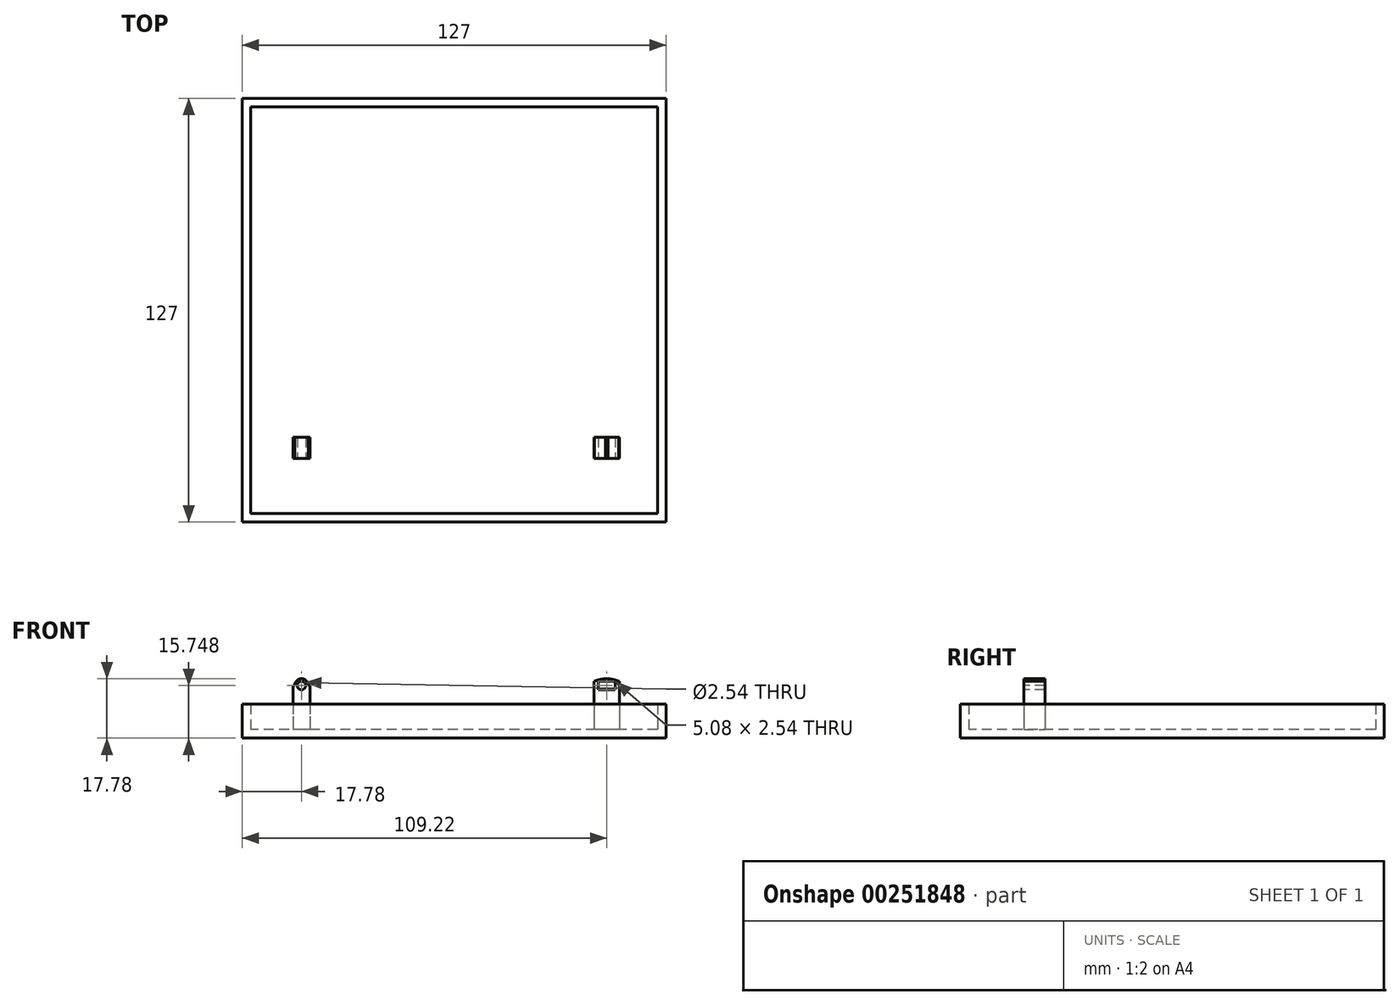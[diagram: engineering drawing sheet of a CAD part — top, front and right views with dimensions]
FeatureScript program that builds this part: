
annotation { "Feature Type Name" : "Feature", "Feature Type Description" : "" }
export const myFeature = defineFeature(function(context is Context, id is Id, definition is map)
    precondition{}
    {
        {
            var Q0;
            Q0=qCreatedBy(makeId("Top.planeOp"),FACE);
            var sketch = newSketch(context, id + "F0", { "sketchPlane" : qUnion([Q0])});
            skLineSegment(sketch, "E0.bottom", {"start": v(63.5, 63.5) * mm, "end": v(-63.5, 63.5) * mm});
            skLineSegment(sketch, "E0.top", {"start": v(63.5, -63.5) * mm, "end": v(-63.5, -63.5) * mm});
            skLineSegment(sketch, "E0.left", {"start": v(63.5, 63.5) * mm, "end": v(63.5, -63.5) * mm});
            skLineSegment(sketch, "E0.right", {"start": v(-63.5, 63.5) * mm, "end": v(-63.5, -63.5) * mm});
            skPoint(sketch, "E0.middle", {"position": v(0, 0) * mm});
            skSolve(sketch);
        }
        {
            var Q0;
            Q0 = qSketchRegion(id + "F0", true);
            extrude(context, id + "F1", {"entities" : qUnion([Q0]), "depth" : 2.54 * mm});
        }
        {
            var Q0;
            Q0=makeQuery(id+"F1.opExtrude","CAP_FACE",FACE,{"disambiguationData":[OSD([sQuery(id+"F0.wireOp",EDGE,"E0.bottom"),sQuery(id+"F0.wireOp",EDGE,"E0.top"),sQuery(id+"F0.wireOp",EDGE,"E0.left"),sQuery(id+"F0.wireOp",EDGE,"E0.right")])],"isStart":false});
            var sketch = newSketch(context, id + "F2", { "sketchPlane" : qUnion([Q0])});
            skLineSegment(sketch, "E1.bottom", {"start": v(63.5, 63.5) * mm, "end": v(-63.5, 63.5) * mm});
            skLineSegment(sketch, "E1.top", {"start": v(63.5, -63.5) * mm, "end": v(-63.5, -63.5) * mm});
            skLineSegment(sketch, "E1.left", {"start": v(63.5, 63.5) * mm, "end": v(63.5, -63.5) * mm});
            skLineSegment(sketch, "E1.right", {"start": v(-63.5, 63.5) * mm, "end": v(-63.5, -63.5) * mm});
            skPoint(sketch, "E1.middle", {"position": v(0, 0) * mm});
            skLineSegment(sketch, "E2.bottom", {"start": v(60.96, 60.96) * mm, "end": v(-60.96, 60.96) * mm});
            skLineSegment(sketch, "E2.top", {"start": v(60.96, -60.96) * mm, "end": v(-60.96, -60.96) * mm});
            skLineSegment(sketch, "E2.left", {"start": v(60.96, 60.96) * mm, "end": v(60.96, -60.96) * mm});
            skLineSegment(sketch, "E2.right", {"start": v(-60.96, 60.96) * mm, "end": v(-60.96, -60.96) * mm});
            skSolve(sketch);
        }
        {
            var Q0;
            Q0 = qSketchRegion(id + "F2", true);
            extrude(context, id + "F3", {"entities" : qUnion([Q0]), "operationType" : NewBodyOperationType.ADD, "depth" : 7.62 * mm});
        }
        {
            var Q0;
            Q0=makeQuery(id+"F1.opExtrude","CAP_FACE",FACE,{"disambiguationData":[OSD([sQuery(id+"F0.wireOp",EDGE,"E0.bottom"),sQuery(id+"F0.wireOp",EDGE,"E0.top"),sQuery(id+"F0.wireOp",EDGE,"E0.left"),sQuery(id+"F0.wireOp",EDGE,"E0.right")])],"isStart":false});
            var sketch = newSketch(context, id + "F4", { "sketchPlane" : qUnion([Q0])});
            skLineSegment(sketch, "E3.bottom", {"start": v(-43.18, -44.45) * mm, "end": v(-48.26, -44.45) * mm});
            skLineSegment(sketch, "E3.top", {"start": v(-43.18, -38.1) * mm, "end": v(-48.26, -38.1) * mm});
            skLineSegment(sketch, "E3.left", {"start": v(-43.18, -44.45) * mm, "end": v(-43.18, -38.1) * mm});
            skLineSegment(sketch, "E3.right", {"start": v(-48.26, -44.45) * mm, "end": v(-48.26, -38.1) * mm});
            skPoint(sketch, "E3.middle", {"position": v(-45.72, -41.27) * mm});
            skLineSegment(sketch, "E4.bottom", {"start": v(49.53, -44.45) * mm, "end": v(41.9, -44.45) * mm});
            skLineSegment(sketch, "E4.top", {"start": v(49.53, -38.1) * mm, "end": v(41.9, -38.1) * mm});
            skLineSegment(sketch, "E4.left", {"start": v(49.53, -44.45) * mm, "end": v(49.53, -38.1) * mm});
            skLineSegment(sketch, "E4.right", {"start": v(41.9, -44.45) * mm, "end": v(41.9, -38.1) * mm});
            skPoint(sketch, "E4.middle", {"position": v(45.72, -41.27) * mm});
            skSolve(sketch);
        }
        {
            var Q0;
            Q0 = qSketchRegion(id + "F4", true);
            extrude(context, id + "F5", {"entities" : qUnion([Q0]), "operationType" : NewBodyOperationType.ADD, "depth" : 15.24 * mm});
        }
        {
            var Q0;
            Q0=makeQuery(id+"F5.opExtrude","SWEPT_FACE",FACE,{"disambiguationData":[OSD([sQuery(id+"F4.wireOp",EDGE,"E3.bottom")])]});
            var sketch = newSketch(context, id + "F6", { "sketchPlane" : qUnion([Q0])});
            skCircle(sketch, "E5", {"center": v(-45.72, 15.75) * mm, "radius": 1.27 * mm});
            skLineSegment(sketch, "E6.bottom", {"start": v(48.26, 17.02) * mm, "end": v(43.18, 17.02) * mm});
            skLineSegment(sketch, "E6.top", {"start": v(48.26, 14.48) * mm, "end": v(43.18, 14.48) * mm});
            skLineSegment(sketch, "E6.left", {"start": v(48.26, 17.02) * mm, "end": v(48.26, 14.48) * mm});
            skLineSegment(sketch, "E6.right", {"start": v(43.18, 17.02) * mm, "end": v(43.18, 14.48) * mm});
            skPoint(sketch, "E6.middle", {"position": v(45.72, 15.75) * mm});
            skArc(sketch, "E7", {"start": v(-45.72, 17.78) * mm, "mid": v(-47.16, 17.18) * mm, "end": v(-47.75, 15.75) * mm});
            skLineSegment(sketch, "E8", {"start": v(-47.75, 15.75) * mm, "end": v(-48.26, 15.75) * mm});
            skLineSegment(sketch, "E9", {"start": v(-48.26, 15.75) * mm, "end": v(-48.26, 17.78) * mm});
            skArc(sketch, "E10", {"start": v(-45.72, 17.78) * mm, "mid": v(-44.28, 17.18) * mm, "end": v(-43.69, 15.75) * mm});
            skLineSegment(sketch, "E11", {"start": v(-43.69, 15.75) * mm, "end": v(-43.18, 15.75) * mm});
            skLineSegment(sketch, "E12", {"start": v(-43.18, 15.75) * mm, "end": v(-43.18, 17.78) * mm});
            skLineSegment(sketch, "E13", {"start": v(-43.18, 17.78) * mm, "end": v(-48.26, 17.78) * mm});
            skPoint(sketch, "E14.startSnap0", {"position": v(45.72, 17.02) * mm});
            skArc(sketch, "E15", {"start": v(45.72, 17.79) * mm, "mid": v(43.87, 17.6) * mm, "end": v(42.1, 17.02) * mm});
            skArc(sketch, "E16", {"start": v(45.72, 17.79) * mm, "mid": v(47.57, 17.6) * mm, "end": v(49.34, 17.02) * mm});
            skLineSegment(sketch, "E17", {"start": v(49.34, 17.02) * mm, "end": v(49.7, 17.02) * mm});
            skLineSegment(sketch, "E18", {"start": v(49.7, 17.02) * mm, "end": v(49.7, 17.79) * mm});
            skLineSegment(sketch, "E19", {"start": v(49.7, 17.79) * mm, "end": v(41.83, 17.79) * mm});
            skLineSegment(sketch, "E20", {"start": v(41.83, 17.79) * mm, "end": v(41.83, 17.02) * mm});
            skLineSegment(sketch, "E21", {"start": v(41.83, 17.02) * mm, "end": v(42.1, 17.02) * mm});
            skSolve(sketch);
        }
        {
            var Q0;
            Q0 = qSketchRegion(id + "F6", true);
            extrude(context, id + "F7", {"entities" : qUnion([Q0]), "operationType" : NewBodyOperationType.REMOVE, "oppositeDirection" : true, "depth" : 6.35 * mm});
        }
    });
